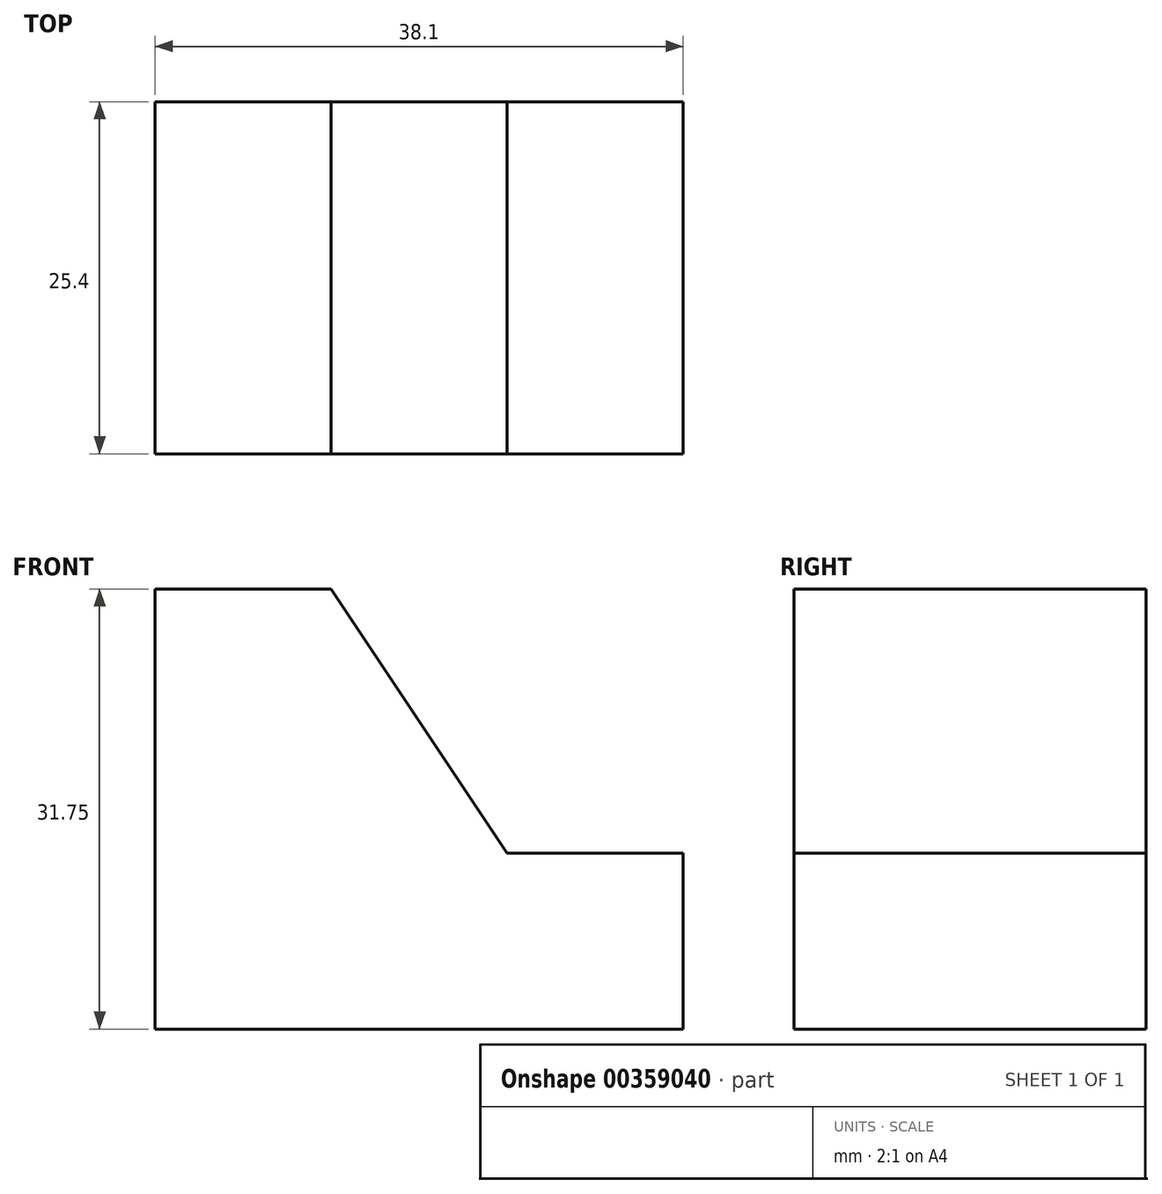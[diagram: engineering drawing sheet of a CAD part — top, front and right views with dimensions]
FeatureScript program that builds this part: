
annotation { "Feature Type Name" : "Feature", "Feature Type Description" : "" }
export const myFeature = defineFeature(function(context is Context, id is Id, definition is map)
    precondition{}
    {
        {
            var Q0;
            Q0=qCreatedBy(makeId("Front.planeOp"),FACE);
            var sketch = newSketch(context, id + "F0", { "sketchPlane" : qUnion([Q0])});
            skLineSegment(sketch, "E0", {"start": v(0, 31.75) * mm, "end": v(12.7, 31.75) * mm});
            skLineSegment(sketch, "E1", {"start": v(12.7, 31.75) * mm, "end": v(25.4, 12.7) * mm});
            skLineSegment(sketch, "E2", {"start": v(25.4, 12.7) * mm, "end": v(38.1, 12.7) * mm});
            skLineSegment(sketch, "E3", {"start": v(38.1, 12.7) * mm, "end": v(38.1, 0) * mm});
            skLineSegment(sketch, "E4", {"start": v(38.1, 0) * mm, "end": v(0, 0) * mm});
            skLineSegment(sketch, "E5", {"start": v(0, 0) * mm, "end": v(0, 31.75) * mm});
            skSolve(sketch);
        }
        {
            var Q0;
            Q0=makeQuery(id+"F0.imprint","IMPRINT",FACE,{"disambiguationData":[TD([[makeQuery(id+"F0.imprint","IMPRINT",EDGE,{"derivedFrom":sQuery(id+"F0.wireOp",EDGE,"E0")}),-1.0]])]});
            extrude(context, id + "F1", {"entities" : qUnion([Q0]), "oppositeDirection" : true, "depth" : 25.4 * mm});
        }
    });
